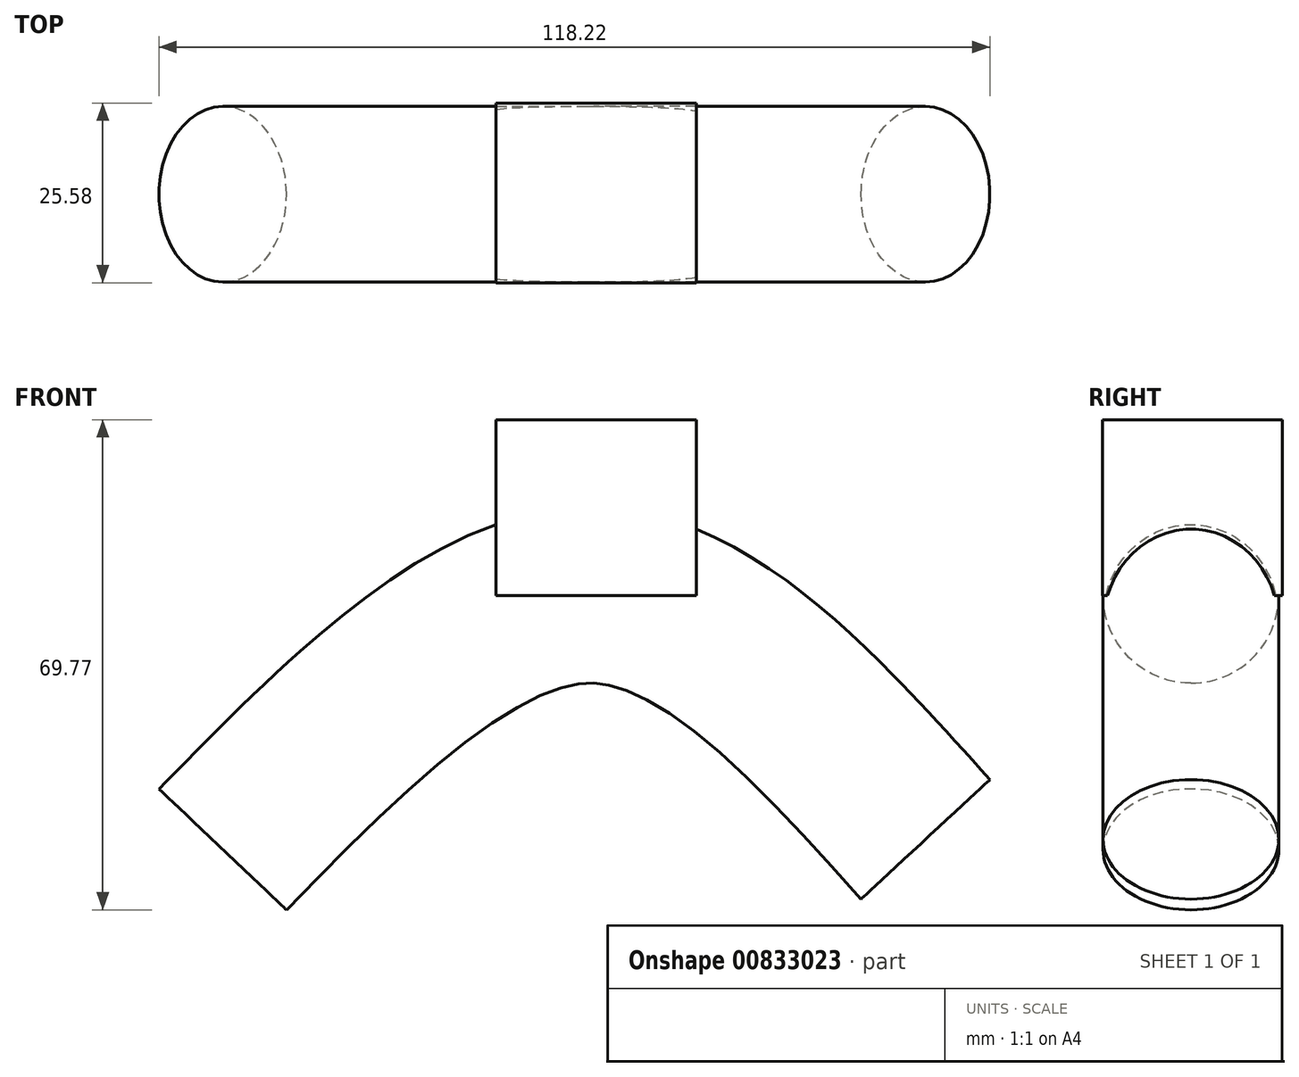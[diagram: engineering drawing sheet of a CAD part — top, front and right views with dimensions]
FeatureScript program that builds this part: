
annotation { "Feature Type Name" : "Feature", "Feature Type Description" : "" }
export const myFeature = defineFeature(function(context is Context, id is Id, definition is map)
    precondition{}
    {
        {
            var Q0;
            Q0=qCreatedBy(makeId("Right.planeOp"),FACE);
            var sketch = newSketch(context, id + "F0", { "sketchPlane" : qUnion([Q0])});
            skCircle(sketch, "E0", {"center": v(0, 0) * mm, "radius": 12.5 * mm});
            skSolve(sketch);
        }
        {
            var Q0;
            Q0=qCreatedBy(makeId("Front.planeOp"),FACE);
            var sketch = newSketch(context, id + "F1", { "sketchPlane" : qUnion([Q0])});
            skFitSpline(sketch, "E1", {"points": [v(-52.77, -36.17) * mm, v(0, 0) * mm, v(47.23, -34.73) * mm], "startDerivative": vector(105, 107.02) * mm, "endDerivative": vector(94.93, -105.7) * mm});
            skSolve(sketch);
        }
        {
            var Q0;
            Q0=makeQuery(id+"F0.imprint","IMPRINT",FACE,{"disambiguationData":[TD([[makeQuery(id+"F0.imprint","IMPRINT",EDGE,{"derivedFrom":sQuery(id+"F0.wireOp",EDGE,"E0")}),1.0]])]});
            var Q1;
            Q1=sQuery(id+"F1.wireOp",EDGE,"E1");
            sweep(context, id + "F2", {"profiles" : qUnion([Q0]), "path" : qUnion([Q1])});
        }
        {
            var Q0;
            Q0=qCreatedBy(makeId("Top.planeOp"),FACE);
            var sketch = newSketch(context, id + "F3", { "sketchPlane" : qUnion([Q0])});
            skLineSegment(sketch, "E2.bottom", {"start": v(-13.88, 12.97) * mm, "end": v(14.6, 12.97) * mm});
            skLineSegment(sketch, "E2.top", {"start": v(-13.88, -12.61) * mm, "end": v(14.6, -12.61) * mm});
            skLineSegment(sketch, "E2.left", {"start": v(-13.88, 12.97) * mm, "end": v(-13.88, -12.61) * mm});
            skLineSegment(sketch, "E2.right", {"start": v(14.6, 12.97) * mm, "end": v(14.6, -12.61) * mm});
            skSolve(sketch);
        }
        {
            var Q0;
            Q0=makeQuery(id+"F3.imprint","IMPRINT",FACE,{"disambiguationData":[TD([[makeQuery(id+"F3.imprint","IMPRINT",EDGE,{"derivedFrom":sQuery(id+"F3.wireOp",EDGE,"E2.bottom")}),-1.0]])]});
            extrude(context, id + "F4", {"entities" : qUnion([Q0]), "operationType" : NewBodyOperationType.ADD, "depth" : 25 * mm, "offsetDistance" : 25 * mm});
        }
    });
